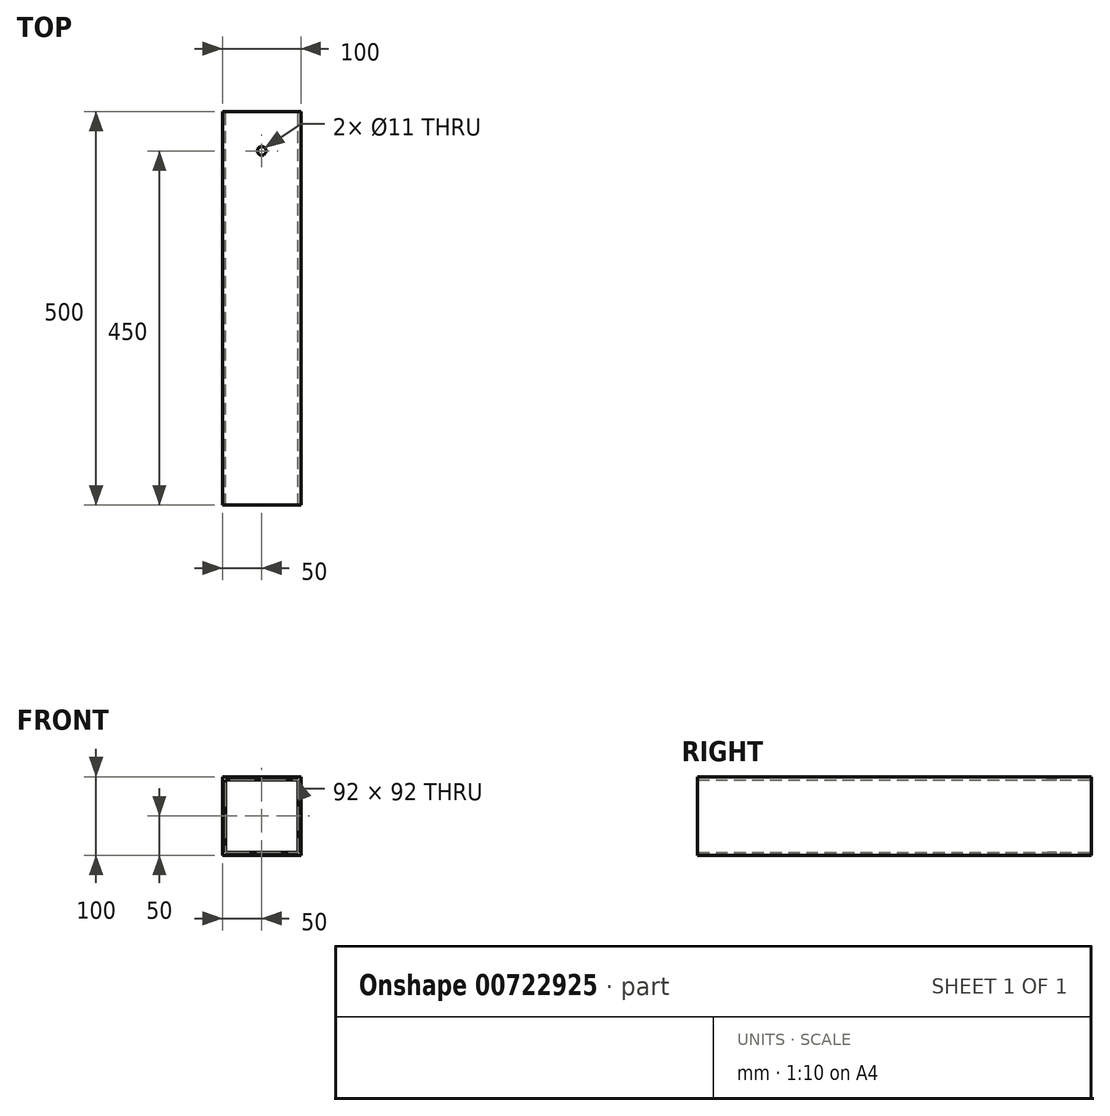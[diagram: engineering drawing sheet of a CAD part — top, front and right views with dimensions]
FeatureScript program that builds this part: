
annotation { "Feature Type Name" : "Feature", "Feature Type Description" : "" }
export const myFeature = defineFeature(function(context is Context, id is Id, definition is map)
    precondition{}
    {
        {
            var Q0;
            Q0=qCreatedBy(makeId("Front.planeOp"),FACE);
            var sketch = newSketch(context, id + "F0", { "sketchPlane" : qUnion([Q0])});
            skLineSegment(sketch, "E0.bottom", {"start": v(0, 0) * mm, "end": v(100, 0) * mm});
            skLineSegment(sketch, "E0.top", {"start": v(0, 100) * mm, "end": v(100, 100) * mm});
            skLineSegment(sketch, "E0.left", {"start": v(0, 0) * mm, "end": v(0, 100) * mm});
            skLineSegment(sketch, "E0.right", {"start": v(100, 0) * mm, "end": v(100, 100) * mm});
            skLineSegment(sketch, "E1.bottom", {"start": v(4, 4) * mm, "end": v(96, 4) * mm});
            skLineSegment(sketch, "E1.top", {"start": v(4, 96) * mm, "end": v(96, 96) * mm});
            skLineSegment(sketch, "E1.left", {"start": v(4, 4) * mm, "end": v(4, 96) * mm});
            skLineSegment(sketch, "E1.right", {"start": v(96, 4) * mm, "end": v(96, 96) * mm});
            skSolve(sketch);
        }
        {
            var Q0;
            Q0=makeQuery(id+"F0.imprint","IMPRINT",FACE,{"disambiguationData":[TD([[makeQuery(id+"F0.imprint","IMPRINT",EDGE,{"derivedFrom":sQuery(id+"F0.wireOp",EDGE,"E0.bottom")}),1.0]])]});
            extrude(context, id + "F1", {"entities" : qUnion([Q0]), "depth" : 500 * mm, "offsetDistance" : 25 * mm});
        }
        {
            var Q0;
            Q0=makeQuery(id+"F1.opExtrude","SWEPT_FACE",FACE,{"disambiguationData":[OSD([sQuery(id+"F0.wireOp",EDGE,"E0.top")])]});
            var sketch = newSketch(context, id + "F2", { "sketchPlane" : qUnion([Q0])});
            skCircle(sketch, "E2", {"center": v(50, -50) * mm, "radius": 5.5 * mm});
            skSolve(sketch);
        }
        {
            var Q0;
            Q0=makeQuery(id+"F2.imprint","IMPRINT",FACE,{"disambiguationData":[TD([[makeQuery(id+"F2.imprint","IMPRINT",EDGE,{"derivedFrom":sQuery(id+"F2.wireOp",EDGE,"E2")}),1.0]])]});
            extrude(context, id + "F3", {"entities" : qUnion([Q0]), "operationType" : NewBodyOperationType.REMOVE, "endBound" : BoundingType.THROUGH_ALL, "oppositeDirection" : true, "depth" : 25 * mm, "offsetDistance" : 25 * mm});
        }
    });
